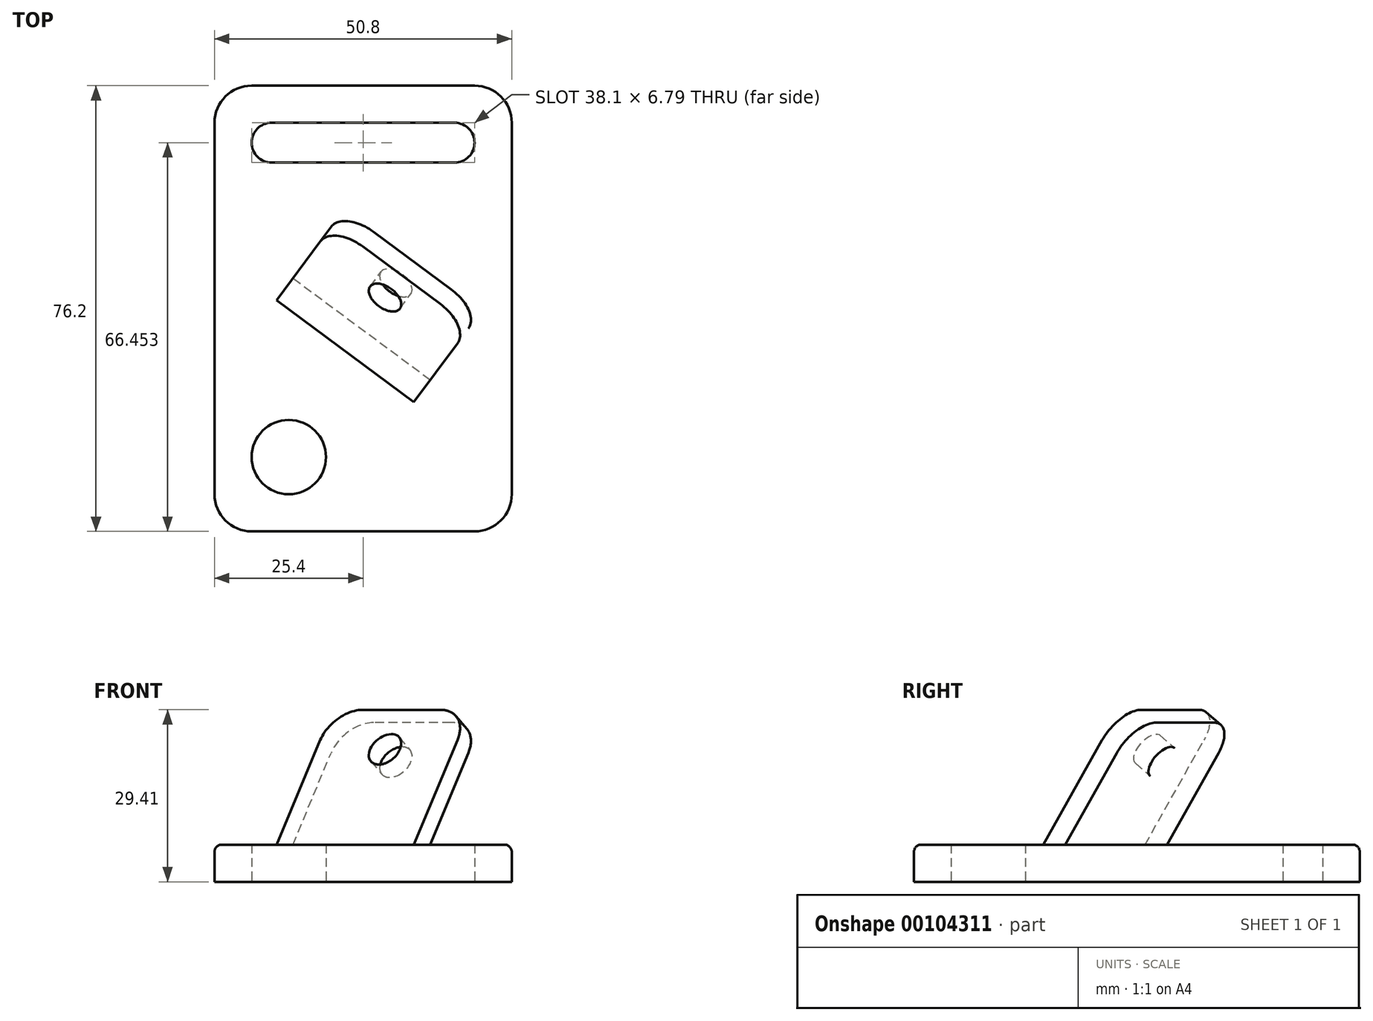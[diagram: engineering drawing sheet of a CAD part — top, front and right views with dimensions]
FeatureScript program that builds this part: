
annotation { "Feature Type Name" : "Feature", "Feature Type Description" : "" }
export const myFeature = defineFeature(function(context is Context, id is Id, definition is map)
    precondition{}
    {
        {
            var Q0;
            Q0=qCreatedBy(makeId("Top.planeOp"),FACE);
            var sketch = newSketch(context, id + "F0", { "sketchPlane" : qUnion([Q0])});
            skLineSegment(sketch, "E0", {"start": v(0, 38.1) * mm, "end": v(19.05, 38.1) * mm});
            skLineSegment(sketch, "E1", {"start": v(25.4, 31.75) * mm, "end": v(25.4, 0) * mm});
            skLineSegment(sketch, "E2.MirrorCS", {"start": v(0, 38.1) * mm, "end": v(-19.05, 38.1) * mm});
            skLineSegment(sketch, "E3.MirrorCS", {"start": v(-25.4, 31.75) * mm, "end": v(-25.4, 0) * mm});
            skLineSegment(sketch, "E4.MirrorCS", {"start": v(-25.4, -31.75) * mm, "end": v(-25.4, 0) * mm});
            skLineSegment(sketch, "E5.MirrorCS", {"start": v(0, -38.1) * mm, "end": v(-19.05, -38.1) * mm});
            skLineSegment(sketch, "E6.MirrorCS", {"start": v(0, -38.1) * mm, "end": v(19.05, -38.1) * mm});
            skLineSegment(sketch, "E7.MirrorCS", {"start": v(25.4, -31.75) * mm, "end": v(25.4, 0) * mm});
            skPoint(sketch, "E8.visualSharp", {"position": v(-25.4, 38.1) * mm});
            skArc(sketch, "E8.filletArc", {"start": v(-19.05, 38.1) * mm, "mid": v(-23.54, 36.24) * mm, "end": v(-25.4, 31.75) * mm});
            skPoint(sketch, "E9.visualSharp", {"position": v(25.4, 38.1) * mm});
            skArc(sketch, "E9.filletArc", {"start": v(25.4, 31.75) * mm, "mid": v(23.54, 36.24) * mm, "end": v(19.05, 38.1) * mm});
            skPoint(sketch, "E10.visualSharp", {"position": v(25.4, -38.1) * mm});
            skArc(sketch, "E10.filletArc", {"start": v(19.05, -38.1) * mm, "mid": v(23.54, -36.24) * mm, "end": v(25.4, -31.75) * mm});
            skPoint(sketch, "E11.visualSharp", {"position": v(-25.4, -38.1) * mm});
            skArc(sketch, "E11.filletArc", {"start": v(-25.4, -31.75) * mm, "mid": v(-23.54, -36.24) * mm, "end": v(-19.05, -38.1) * mm});
            skCircle(sketch, "E12", {"center": v(-12.7, -25.4) * mm, "radius": 6.35 * mm});
            skLineSegment(sketch, "E13", {"start": v(0, 31.75) * mm, "end": v(-15.65, 31.75) * mm});
            skLineSegment(sketch, "E14", {"start": v(0, 24.96) * mm, "end": v(-15.65, 24.96) * mm});
            skArc(sketch, "E15", {"start": v(-15.65, 31.75) * mm, "mid": v(-19.05, 28.35) * mm, "end": v(-15.65, 24.96) * mm});
            skLineSegment(sketch, "E16.MirrorCS", {"start": v(0, 31.75) * mm, "end": v(15.65, 31.75) * mm});
            skArc(sketch, "E17.MirrorCS", {"start": v(15.65, 31.75) * mm, "mid": v(19.05, 28.35) * mm, "end": v(15.65, 24.96) * mm});
            skLineSegment(sketch, "E18.MirrorCS", {"start": v(0, 24.96) * mm, "end": v(15.65, 24.96) * mm});
            skLineSegment(sketch, "E19", {"start": v(-12.7, 0) * mm, "end": v(7.7, -15.13) * mm, "construction": true});
            skSolve(sketch);
        }
        {
            var Q0;
            Q0=sQuery(id+"F0.wireOp",EDGE,"E19");
            cPlane(context, id + "F1", {"entities" : qUnion([Q0]), "cplaneType" : CPlaneType.LINE_ANGLE, "offset" : 152.4 * mm, "angle" : 145 * degree, "width" : 152.4 * mm, "height" : 152.4 * mm});
        }
        {
            var Q0;
            Q0=qCreatedBy(id+"F1.planeOp",FACE);
            var sketch = newSketch(context, id + "F2", { "sketchPlane" : qUnion([Q0])});
            skLineSegment(sketch, "E20", {"start": v(-13.81, 0) * mm, "end": v(13.07, -11.43) * mm});
            skLineSegment(sketch, "E21", {"start": v(13.07, -11.43) * mm, "end": v(23, 11.94) * mm});
            skLineSegment(sketch, "E22", {"start": v(-13.81, 0) * mm, "end": v(-3.87, 23.37) * mm});
            skLineSegment(sketch, "E23", {"start": v(19.65, 20.27) * mm, "end": v(4.46, 26.73) * mm});
            skPoint(sketch, "E24.visualSharp", {"position": v(-1.39, 29.22) * mm});
            skArc(sketch, "E24.filletArc", {"start": v(4.46, 26.73) * mm, "mid": v(-0.4, 26.78) * mm, "end": v(-3.87, 23.37) * mm});
            skPoint(sketch, "E25.visualSharp", {"position": v(25.5, 17.79) * mm});
            skArc(sketch, "E25.filletArc", {"start": v(23, 11.94) * mm, "mid": v(23.05, 16.8) * mm, "end": v(19.65, 20.27) * mm});
            skCircle(sketch, "E26", {"center": v(8.82, 15.9) * mm, "radius": 3.18 * mm});
            skSolve(sketch);
        }
        {
            var Q0;
            Q0 = qSketchRegion(id + "F2", true);
            extrude(context, id + "F3", {"entities" : qUnion([Q0]), "endBound" : BoundingType.SYMMETRIC, "depth" : 3.8 * mm});
        }
        {
            var Q0;
            Q0 = qSketchRegion(id + "F0", true);
            extrude(context, id + "F4", {"entities" : qUnion([Q0]), "operationType" : NewBodyOperationType.ADD, "endBound" : BoundingType.SYMMETRIC, "depth" : 6.35 * mm});
        }
        {
            var Q0;
            Q0=makeQuery(id+"F4.opExtrude","CAP_EDGE",EDGE,{"disambiguationData":[OSD([sQuery(id+"F0.wireOp",EDGE,"E0"),sQuery(id+"F0.wireOp",EDGE,"E2.MirrorCS")])],"isStart":false});
            var Q1;
            Q1=makeQuery(id+"F4.opExtrude","CAP_EDGE",EDGE,{"disambiguationData":[OSD([sQuery(id+"F0.wireOp",EDGE,"E8.filletArc")])],"isStart":false});
            var Q2;
            Q2=makeQuery(id+"F4.opExtrude","CAP_EDGE",EDGE,{"disambiguationData":[OSD([sQuery(id+"F0.wireOp",EDGE,"E3.MirrorCS"),sQuery(id+"F0.wireOp",EDGE,"E4.MirrorCS")])],"isStart":false});
            var Q3;
            Q3=makeQuery(id+"F4.opExtrude","CAP_EDGE",EDGE,{"disambiguationData":[OSD([sQuery(id+"F0.wireOp",EDGE,"E11.filletArc")])],"isStart":false});
            var Q4;
            Q4=makeQuery(id+"F4.opExtrude","CAP_EDGE",EDGE,{"disambiguationData":[OSD([sQuery(id+"F0.wireOp",EDGE,"E5.MirrorCS"),sQuery(id+"F0.wireOp",EDGE,"E6.MirrorCS")])],"isStart":false});
            var Q5;
            Q5=makeQuery(id+"F4.opExtrude","CAP_EDGE",EDGE,{"disambiguationData":[OSD([sQuery(id+"F0.wireOp",EDGE,"E10.filletArc")])],"isStart":false});
            var Q6;
            Q6=makeQuery(id+"F4.opExtrude","CAP_EDGE",EDGE,{"disambiguationData":[OSD([sQuery(id+"F0.wireOp",EDGE,"E1"),sQuery(id+"F0.wireOp",EDGE,"E7.MirrorCS")])],"isStart":false});
            var Q7;
            Q7=makeQuery(id+"F4.opExtrude","CAP_EDGE",EDGE,{"disambiguationData":[OSD([sQuery(id+"F0.wireOp",EDGE,"E9.filletArc")])],"isStart":false});
            fillet(context, id + "F5", {"entities" : qUnion([Q0, Q1, Q2, Q3, Q4, Q5, Q6, Q7]), "radius" : 1.27 * mm, "tangentPropagation" : true, "allowEdgeOverflow" : false});
        }
    });
